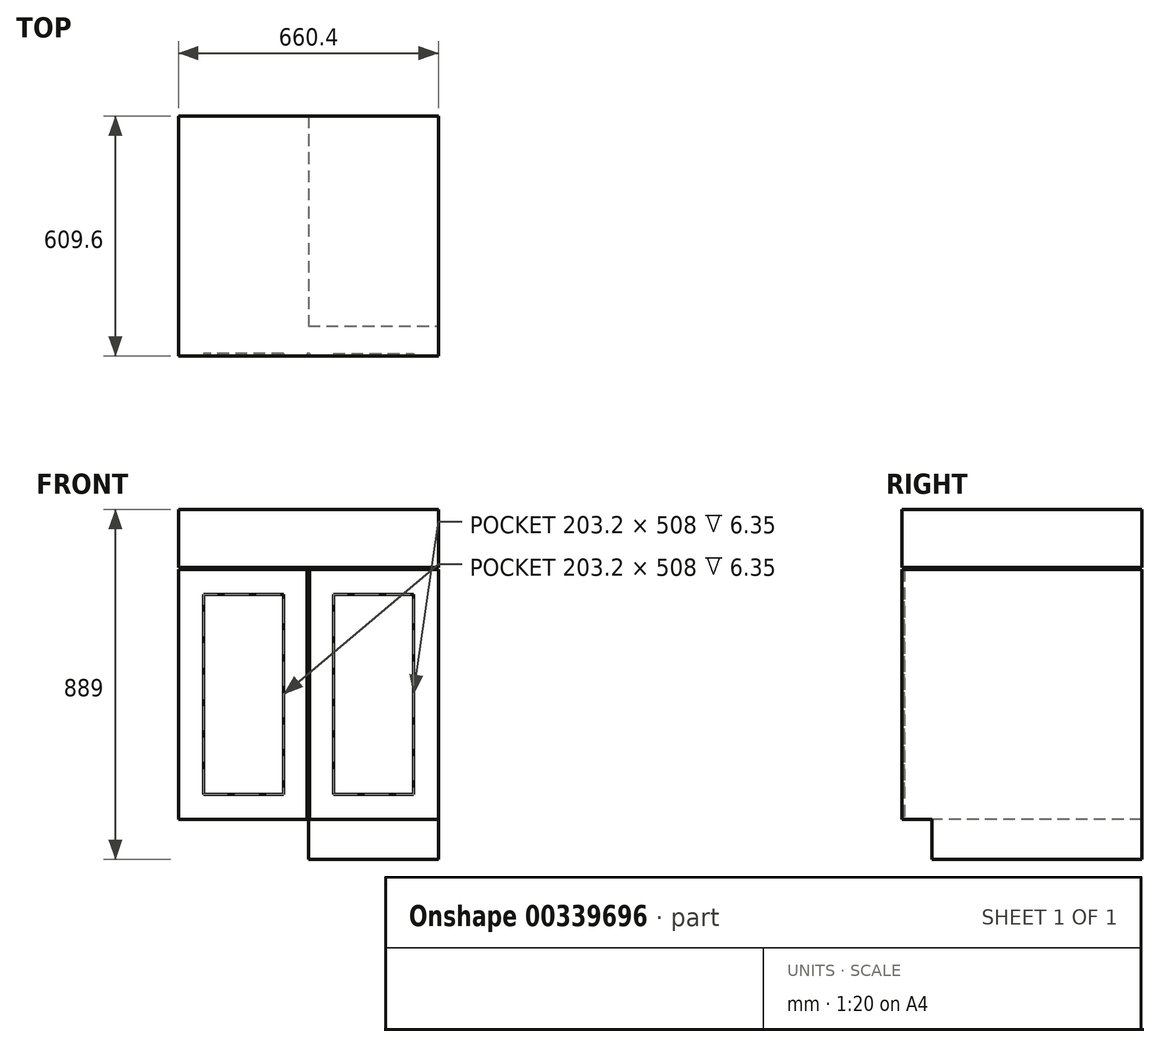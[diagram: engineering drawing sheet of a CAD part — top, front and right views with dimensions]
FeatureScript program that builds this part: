
annotation { "Feature Type Name" : "Feature", "Feature Type Description" : "" }
export const myFeature = defineFeature(function(context is Context, id is Id, definition is map)
    precondition{}
    {
        {
            var Q0;
            Q0=qCreatedBy(makeId("Front.planeOp"),FACE);
            var sketch = newSketch(context, id + "F0", { "sketchPlane" : qUnion([Q0])});
            skLineSegment(sketch, "E0.bottom", {"start": v(227.9, 0) * mm, "end": v(-102.3, 0) * mm});
            skLineSegment(sketch, "E0.top", {"start": v(227.9, 635) * mm, "end": v(-102.3, 635) * mm});
            skLineSegment(sketch, "E0.left", {"start": v(227.9, 0) * mm, "end": v(227.9, 635) * mm});
            skLineSegment(sketch, "E0.right", {"start": v(-102.3, 0) * mm, "end": v(-102.3, 635) * mm});
            skLineSegment(sketch, "E1.0", {"start": v(164.4, 571.5) * mm, "end": v(-38.8, 571.5) * mm});
            skLineSegment(sketch, "E1.1", {"start": v(164.4, 63.5) * mm, "end": v(164.4, 571.5) * mm});
            skLineSegment(sketch, "E1.2", {"start": v(164.4, 63.5) * mm, "end": v(-38.8, 63.5) * mm});
            skLineSegment(sketch, "E1.3", {"start": v(-38.8, 63.5) * mm, "end": v(-38.8, 571.5) * mm});
            skLineSegment(sketch, "E2.bottom", {"start": v(-102.3, 0) * mm, "end": v(227.9, 0) * mm});
            skLineSegment(sketch, "E2.top", {"start": v(-102.3, -101.6) * mm, "end": v(227.9, -101.6) * mm});
            skLineSegment(sketch, "E2.left", {"start": v(-102.3, 0) * mm, "end": v(-102.3, -101.6) * mm});
            skLineSegment(sketch, "E2.right", {"start": v(227.9, 0) * mm, "end": v(227.9, -101.6) * mm});
            skLineSegment(sketch, "E3.bottom", {"start": v(-102.3, 635) * mm, "end": v(227.9, 635) * mm});
            skLineSegment(sketch, "E3.top", {"start": v(-102.3, 787.4) * mm, "end": v(227.9, 787.4) * mm});
            skLineSegment(sketch, "E3.left", {"start": v(-102.3, 635) * mm, "end": v(-102.3, 787.4) * mm});
            skLineSegment(sketch, "E3.right", {"start": v(227.9, 635) * mm, "end": v(227.9, 787.4) * mm});
            skLineSegment(sketch, "E4.top", {"start": v(-102.3, 640.08) * mm, "end": v(227.9, 640.08) * mm});
            skLineSegment(sketch, "E4.left", {"start": v(-102.3, 635) * mm, "end": v(-102.3, 640.08) * mm});
            skLineSegment(sketch, "E4.right", {"start": v(227.9, 635) * mm, "end": v(227.9, 640.08) * mm});
            skLineSegment(sketch, "E5.MirrorCS", {"start": v(558.1, 635) * mm, "end": v(558.1, 640.08) * mm});
            skLineSegment(sketch, "E6.MirrorCS", {"start": v(227.9, 635) * mm, "end": v(558.1, 635) * mm});
            skLineSegment(sketch, "E7.MirrorCS", {"start": v(558.1, 635) * mm, "end": v(227.9, 635) * mm});
            skLineSegment(sketch, "E8.MirrorCS", {"start": v(227.9, 0) * mm, "end": v(558.1, 0) * mm});
            skLineSegment(sketch, "E9.MirrorCS", {"start": v(558.1, 0) * mm, "end": v(558.1, -101.6) * mm});
            skLineSegment(sketch, "E10.MirrorCS", {"start": v(558.1, -101.6) * mm, "end": v(227.9, -101.6) * mm});
            skLineSegment(sketch, "E11.MirrorCS", {"start": v(558.1, 0) * mm, "end": v(227.9, 0) * mm});
            skLineSegment(sketch, "E12.MirrorCS", {"start": v(494.6, 63.5) * mm, "end": v(494.6, 571.5) * mm});
            skLineSegment(sketch, "E13.MirrorCS", {"start": v(291.4, 63.5) * mm, "end": v(494.6, 63.5) * mm});
            skLineSegment(sketch, "E14.MirrorCS", {"start": v(291.4, 63.5) * mm, "end": v(291.4, 571.5) * mm});
            skLineSegment(sketch, "E15.MirrorCS", {"start": v(291.4, 571.5) * mm, "end": v(494.6, 571.5) * mm});
            skLineSegment(sketch, "E16.MirrorCS", {"start": v(558.1, 0) * mm, "end": v(558.1, 635) * mm});
            skLineSegment(sketch, "E17.MirrorCS", {"start": v(558.1, 635) * mm, "end": v(558.1, 787.4) * mm});
            skLineSegment(sketch, "E18.MirrorCS", {"start": v(558.1, 640.08) * mm, "end": v(227.9, 640.08) * mm});
            skLineSegment(sketch, "E19.MirrorCS", {"start": v(558.1, 787.4) * mm, "end": v(227.9, 787.4) * mm});
            skLineSegment(sketch, "E20", {"start": v(224.73, 635) * mm, "end": v(224.73, 0) * mm});
            skLineSegment(sketch, "E21", {"start": v(231.08, 635) * mm, "end": v(231.08, 0) * mm});
            skSolve(sketch);
        }
        {
            var Q0;
            Q0=makeQuery(id+"F0.imprint","IMPRINT",FACE,{"disambiguationData":[TD([[makeQuery(id+"F0.imprint","IMPRINT",EDGE,{"derivedFrom":sQuery(id+"F0.wireOp",EDGE,"E1.0")}),1.0]])]});
            var Q1;
            Q1=makeQuery(id+"F0.imprint","IMPRINT",FACE,{"disambiguationData":[TD([[makeQuery(id+"F0.imprint","IMPRINT",EDGE,{"derivedFrom":sQuery(id+"F0.wireOp",EDGE,"E2.bottom")}),-1.0]])]});
            var Q2;
            Q2=makeQuery(id+"F0.imprint","IMPRINT",FACE,{"disambiguationData":[TD([[makeQuery(id+"F0.imprint","IMPRINT",EDGE,{"derivedFrom":sQuery(id+"F0.wireOp",EDGE,"E0.left")}),1.0]])]});
            var Q3;
            {var subQ0=sQuery(id+"F0.wireOp",EDGE,"E3.top");Q3=makeQuery(id+"F0.imprint","IMPRINT",FACE,{"disambiguationData":[TD([[makeQuery(id+"F0.imprint","IMPRINT",EDGE,{"derivedFrom":subQ0}),-1.0]])]});}
            var Q4;
            {var subQ0=sQuery(id+"F0.wireOp",EDGE,"E3.bottom");Q4=makeQuery(id+"F0.imprint","IMPRINT",FACE,{"disambiguationData":[TD([[makeQuery(id+"F0.imprint","IMPRINT",EDGE,{"derivedFrom":subQ0}),1.0]])]});}
            var Q5;
            Q5=makeQuery(id+"F0.imprint","IMPRINT",FACE,{"disambiguationData":[TD([[makeQuery(id+"F0.imprint","IMPRINT",EDGE,{"derivedFrom":sQuery(id+"F0.wireOp",EDGE,"E12.MirrorCS")}),1.0]])]});
            var Q6;
            {var subQ2=sQuery(id+"F0.wireOp",EDGE,"E18.MirrorCS");Q6=makeQuery(id+"F0.imprint","IMPRINT",FACE,{"disambiguationData":[TD([[makeQuery(id+"F0.imprint","IMPRINT",EDGE,{"derivedFrom":subQ2}),-1.0]])]});}
            var Q7;
            Q7=makeQuery(id+"F0.imprint","IMPRINT",FACE,{"disambiguationData":[TD([[makeQuery(id+"F0.imprint","IMPRINT",EDGE,{"derivedFrom":sQuery(id+"F0.wireOp",EDGE,"E2.right")}),1.0]])]});
            var Q8;
            Q8=makeQuery(id+"F0.imprint","IMPRINT",FACE,{"disambiguationData":[TD([[makeQuery(id+"F0.imprint","IMPRINT",EDGE,{"derivedFrom":sQuery(id+"F0.wireOp",EDGE,"E0.left")}),-1.0]])]});
            var Q9;
            {var subQ0=sQuery(id+"F0.wireOp",EDGE,"E7.MirrorCS");Q9=makeQuery(id+"F0.imprint","IMPRINT",FACE,{"disambiguationData":[TD([[makeQuery(id+"F0.imprint","IMPRINT",EDGE,{"derivedFrom":subQ0}),-1.0]])]});}
            var Q10;
            {var subQ0=sQuery(id+"F0.wireOp",EDGE,"E0.right");Q10=makeQuery(id+"F0.imprint","IMPRINT",FACE,{"disambiguationData":[TD([[makeQuery(id+"F0.imprint","IMPRINT",EDGE,{"derivedFrom":subQ0}),-1.0]])]});}
            var Q11;
            Q11=makeQuery(id+"F0.imprint","IMPRINT",FACE,{"disambiguationData":[TD([[makeQuery(id+"F0.imprint","IMPRINT",EDGE,{"derivedFrom":sQuery(id+"F0.wireOp",EDGE,"E12.MirrorCS")}),-1.0]])]});
            extrude(context, id + "F1", {"entities" : qUnion([Q0, Q1, Q2, Q3, Q4, Q5, Q6, Q7, Q8, Q9, Q10, Q11]), "oppositeDirection" : true, "depth" : 609.6 * mm});
        }
        {
            var Q0;
            Q0=makeQuery(id+"F0.imprint","IMPRINT",FACE,{"disambiguationData":[TD([[makeQuery(id+"F0.imprint","IMPRINT",EDGE,{"derivedFrom":sQuery(id+"F0.wireOp",EDGE,"E1.0")}),1.0]])]});
            var Q1;
            Q1=makeQuery(id+"F0.imprint","IMPRINT",FACE,{"disambiguationData":[TD([[makeQuery(id+"F0.imprint","IMPRINT",EDGE,{"derivedFrom":sQuery(id+"F0.wireOp",EDGE,"E3.bottom")}),1.0]])]});
            var Q2;
            Q2=makeQuery(id+"F0.imprint","IMPRINT",FACE,{"disambiguationData":[TD([[makeQuery(id+"F0.imprint","IMPRINT",EDGE,{"derivedFrom":sQuery(id+"F0.wireOp",EDGE,"E12.MirrorCS")}),1.0]])]});
            var Q3;
            {var subQ0=sQuery(id+"F0.wireOp",EDGE,"E7.MirrorCS");Q3=makeQuery(id+"F0.imprint","IMPRINT",FACE,{"disambiguationData":[TD([[makeQuery(id+"F0.imprint","IMPRINT",EDGE,{"derivedFrom":subQ0}),-1.0]])]});}
            var Q4;
            {var subQ0=sQuery(id+"F0.wireOp",EDGE,"E0.left");Q4=makeQuery(id+"F0.imprint","IMPRINT",FACE,{"disambiguationData":[TD([[makeQuery(id+"F0.imprint","IMPRINT",EDGE,{"derivedFrom":subQ0}),1.0]])]});}
            var Q5;
            {var subQ0=sQuery(id+"F0.wireOp",EDGE,"E0.left");Q5=makeQuery(id+"F0.imprint","IMPRINT",FACE,{"disambiguationData":[TD([[makeQuery(id+"F0.imprint","IMPRINT",EDGE,{"derivedFrom":subQ0}),-1.0]])]});}
            extrude(context, id + "F2", {"entities" : qUnion([Q0, Q1, Q2, Q3, Q4, Q5]), "operationType" : NewBodyOperationType.REMOVE, "oppositeDirection" : true, "depth" : 6.35 * mm});
        }
        {
            var Q0;
            Q0=makeQuery(id+"F0.imprint","IMPRINT",FACE,{"disambiguationData":[TD([[makeQuery(id+"F0.imprint","IMPRINT",EDGE,{"derivedFrom":sQuery(id+"F0.wireOp",EDGE,"E2.bottom")}),-1.0]])]});
            var Q1;
            Q1=makeQuery(id+"F0.imprint","IMPRINT",FACE,{"disambiguationData":[TD([[makeQuery(id+"F0.imprint","IMPRINT",EDGE,{"derivedFrom":sQuery(id+"F0.wireOp",EDGE,"E2.right")}),1.0]])]});
            extrude(context, id + "F3", {"entities" : qUnion([Q0, Q1]), "operationType" : NewBodyOperationType.REMOVE, "oppositeDirection" : true, "depth" : 76.2 * mm});
        }
    });
